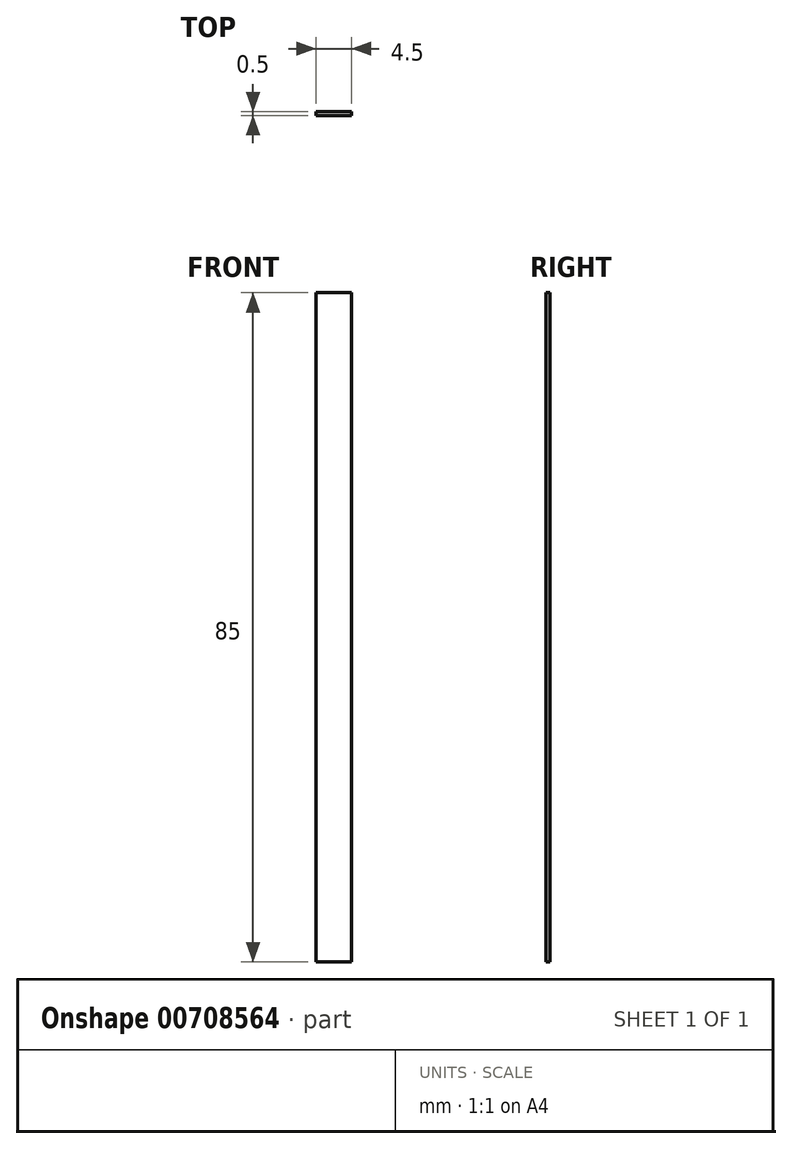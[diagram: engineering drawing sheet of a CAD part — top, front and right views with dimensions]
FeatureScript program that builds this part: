
annotation { "Feature Type Name" : "Feature", "Feature Type Description" : "" }
export const myFeature = defineFeature(function(context is Context, id is Id, definition is map)
    precondition{}
    {
        {
            var Q0;
            Q0=qCreatedBy(makeId("Front.planeOp"),FACE);
            var sketch = newSketch(context, id + "F0", { "sketchPlane" : qUnion([Q0])});
            skLineSegment(sketch, "E0.bottom", {"start": v(-2.36, 60.04) * mm, "end": v(2.14, 60.04) * mm});
            skLineSegment(sketch, "E0.top", {"start": v(-2.36, -24.96) * mm, "end": v(2.14, -24.96) * mm});
            skLineSegment(sketch, "E0.left", {"start": v(-2.36, 60.04) * mm, "end": v(-2.36, -24.96) * mm});
            skLineSegment(sketch, "E0.right", {"start": v(2.14, 60.04) * mm, "end": v(2.14, -24.96) * mm});
            skSolve(sketch);
        }
        {
            var Q0;
            Q0=qSketchRegion(id+"F0",true);
            extrude(context, id + "F1", {"entities" : qUnion([Q0]), "depth" : 0.5 * mm, "offsetDistance" : 25 * mm});
        }
    });
